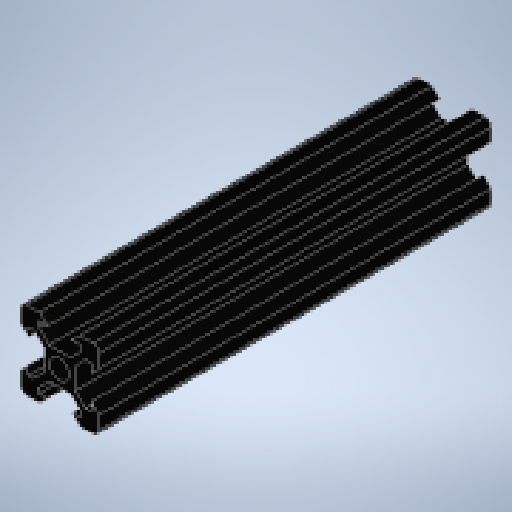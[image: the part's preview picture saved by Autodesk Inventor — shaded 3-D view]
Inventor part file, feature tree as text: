
AUTODESK INVENTOR PART (.ipt)
format: ipt  version: 2025.1 (Build 291241020, 241B)  size: 394,752 bytes
history: native  units: in
note: dims shown in document units (in); Inventor stores cm internally (conversion verified against a paired STEP export)
features: extrude x2, sketch x1, projected_geometry x1, other x1
ambient origin geometry x8: Origin, YZ Plane, XZ Plane, XY Plane, X Axis, Y Axis, Z Axis, Center Point
bodies: Solid1 (feature_tree)
feature tree (5):
  sketch  "Sketch1"  dims[d0=3.937in d1=0.0in d2=3.937in d3=0.0in]
  extrude  "Extrusion1"  Depth=3.937in TaperAngle=0.0deg
  extrude  "Extrusion2"  [1 undecoded]
  projected_geometry  "Projected Loop1"
  other  "Скругление1"
note: 1 required parameter value undecoded (feature->parameter linkage not recoverable at this tier; creation-order binding heuristic only, values carry confidence <= 0.55)
